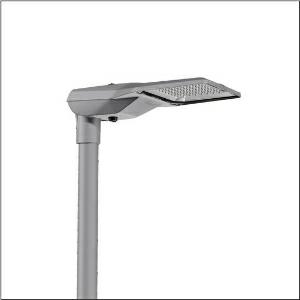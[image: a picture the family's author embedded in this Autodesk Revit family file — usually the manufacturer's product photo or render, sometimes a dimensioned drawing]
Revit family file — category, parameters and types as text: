
# Revit family: streetlight_sl_21_midi___st1_0ab_5xe3m33t08mb_b6c0
name_source: partatom
category: Lighting Fixtures
units: mm (PartAtom-declared; Revit-internal decimal feet)

## family parameters
Cut with Voids When Loaded = No
Host = Face
Light Source = No
Part Type = Normal
Room Calculation Point = No
Round Connector Dimension = Use Diameter
Shared = No

## types (1)
- --- (1 x LED, 16080 lm, 136 W, 3000K)
    Apparent Load = 136 VA
    CIE Flux Codes = 38 73 97 100 100
    Color Rendering = 70
    Color Temperature = 3000K
    Default Elevation = 1800 mm
    Description = Streetlight SL 21 midi, mast luminaire, primary light control with lens, of PMMA, primary optical cover: cover, of toughened safety glass, transparent, light distribution: ST1.0aB, light emission: direct distribution, primary light characteristic: asymmetric, installation type: side-entry, post-top, LED, High Power LED, rated luminous flux: 16.080lm, luminous efficacy: 118lm/W, light colour: 730, colour temperature: 3000K, control gear: D4i, control: flexible luminous flux parameterisation, time-dependent luminous flux control, constant luminous flux control, overheat protection, pre-setting: logarithmic dimming characteristic, mains connection: 230..240V, AC, 50/60Hz, start of lifetime: 136W, end of service life: 142W, reduction: 61W, luminaire housing, of diecast aluminium, powder-coated, SITECO metallic grey (DB 702S), corrosivity category C5 high according to DIN EN ISO 12944, please order mast flange separately, inclination adjustable: 0°, 5°, 10°, 15°, sealing non-destructively replaceable, multi-level sealing system, length: 644mm, width: 335mm, height: 110mm, mast flange for spigot size: 42mm (side-entry): 5XC10008XM4, 60/48mm (side-entry/post-top): 5XC10108XM2, 76/60mm (side-entry/post-top): 5XC10108XM1, mounting height: 4..8m, Smart Interface below and above, protection rating (complete): IP66, insulation class (complete): insulation class II (safety insulation), certification: CE, ENEC, ENEC+, VDE, impact resistance: IK10, permissible operating ambient temperature for outdoor applications: -40..+50°C, standard-compliant lighting for roads and squares, packaging unit: 1 piece

Light Distribution: ST1.0aB
    Height = 111 mm
    Lamp = 1 x LED
    Lamp Light Flux = 16080 lm
    Lamp Power = 136 W
    Lamp count = 1
    Length = 644 mm
    Luminous efficacy = 118 lm/W
    Manufacturer = Siteco
    ModVariant = No
    Model = 5XE3M33T08MB
    Number of Poles = 1
    OnlyDefault = Yes
    Power Factor = 1
    Product Name = Streetlight SL 21 midi | ST1.0aB
    Product group = mast luminaire | pylon top
    ProductGroupID = 6100
    Protection Class = Protection class II
    Protection Degree = IP 66
    RLX_Detail_Level = 1
    RLX_Emergency_Light_Flux = 0 lm
    RLX_Emergency_Type = 0
    RLX_Emergency_Type_DB = No
    RlxData = <blob elided: 27001 chars, md5=3bf80355>
    Socket = socket
    Standby Power = 0 W
    System Light Flux = 16081 lm
    System Power = 136 W
    Type Comments = factory setting: luminous flux: 100 % | dim-lin: 254 | 695 mA
    Type Image = l_1004304.jpg
    URL = http://relux.com
    VarID = @adj_180347
    Voltage = 0 V
    Weight = 0.00 kg
    Width = 336 mm

## geometry (parser evidence)
native form markers: Blend x4, Sweep x12
no freeform markers — native parametric forms only
